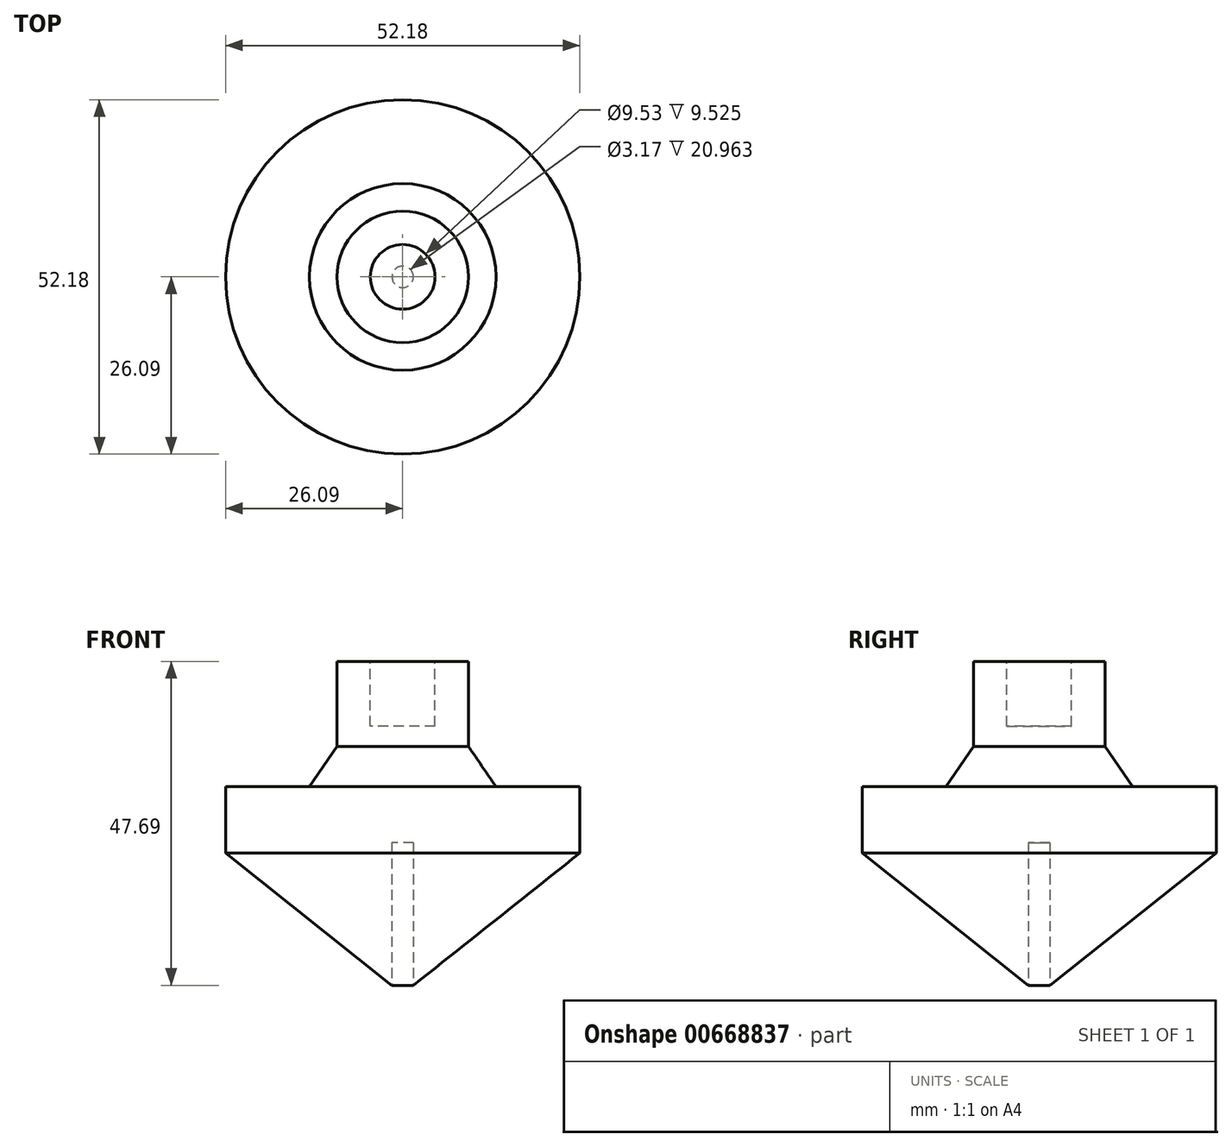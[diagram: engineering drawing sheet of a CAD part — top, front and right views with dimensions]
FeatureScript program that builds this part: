
annotation { "Feature Type Name" : "Feature", "Feature Type Description" : "" }
export const myFeature = defineFeature(function(context is Context, id is Id, definition is map)
    precondition{}
    {
        {
            var Q0;
            Q0=qCreatedBy(makeId("Front.planeOp"),FACE);
            var sketch = newSketch(context, id + "F0", { "sketchPlane" : qUnion([Q0])});
            skLineSegment(sketch, "E0", {"start": v(0, 0) * mm, "end": v(26.09, 20.74) * mm});
            skLineSegment(sketch, "E1", {"start": v(26.09, 20.74) * mm, "end": v(26.09, 30.51) * mm});
            skLineSegment(sketch, "E2", {"start": v(26.09, 30.51) * mm, "end": v(13.73, 30.51) * mm});
            skLineSegment(sketch, "E3", {"start": v(13.73, 30.51) * mm, "end": v(9.68, 36.41) * mm});
            skLineSegment(sketch, "E4", {"start": v(9.68, 36.41) * mm, "end": v(9.68, 48.95) * mm});
            skLineSegment(sketch, "E5", {"start": v(9.68, 48.95) * mm, "end": v(0, 48.95) * mm});
            skLineSegment(sketch, "E6", {"start": v(0, 48.95) * mm, "end": v(0, 0) * mm});
            skSolve(sketch);
        }
        {
            var Q0;
            Q0 = qSketchRegion(id + "F0", true);
            var Q1;
            Q1=sQuery(id+"F0.wireOp",EDGE,"E6");
            revolve(context, id + "F1", {"entities" : qUnion([Q0]), "axis" : qUnion([Q1]), "revolveType" : RevolveType.FULL});
        }
        {
            var Q0;
            Q0=makeQuery(id+"F1.opRevolve","SWEPT_FACE",FACE,{"disambiguationData":[OSD([sQuery(id+"F0.wireOp",EDGE,"E5")])]});
            var sketch = newSketch(context, id + "F2", { "sketchPlane" : qUnion([Q0])});
            skCircle(sketch, "E7", {"center": v(0, 0) * mm, "radius": 4.76 * mm});
            skSolve(sketch);
        }
        {
            var Q0;
            Q0 = qSketchRegion(id + "F2", true);
            extrude(context, id + "F3", {"entities" : qUnion([Q0]), "operationType" : NewBodyOperationType.REMOVE, "oppositeDirection" : true, "depth" : 9.52 * mm, "offsetDistance" : 25.4 * mm});
        }
        {
            var Q0;
            Q0=qCreatedBy(makeId("Top.planeOp"),FACE);
            var sketch = newSketch(context, id + "F4", { "sketchPlane" : qUnion([Q0])});
            skCircle(sketch, "E8", {"center": v(0, 0) * mm, "radius": 1.59 * mm});
            skSolve(sketch);
        }
        {
            var Q0;
            Q0 = qSketchRegion(id + "F4", true);
            extrude(context, id + "F5", {"entities" : qUnion([Q0]), "operationType" : NewBodyOperationType.REMOVE, "depth" : 22.22 * mm, "offsetDistance" : 25.4 * mm});
        }
    });
